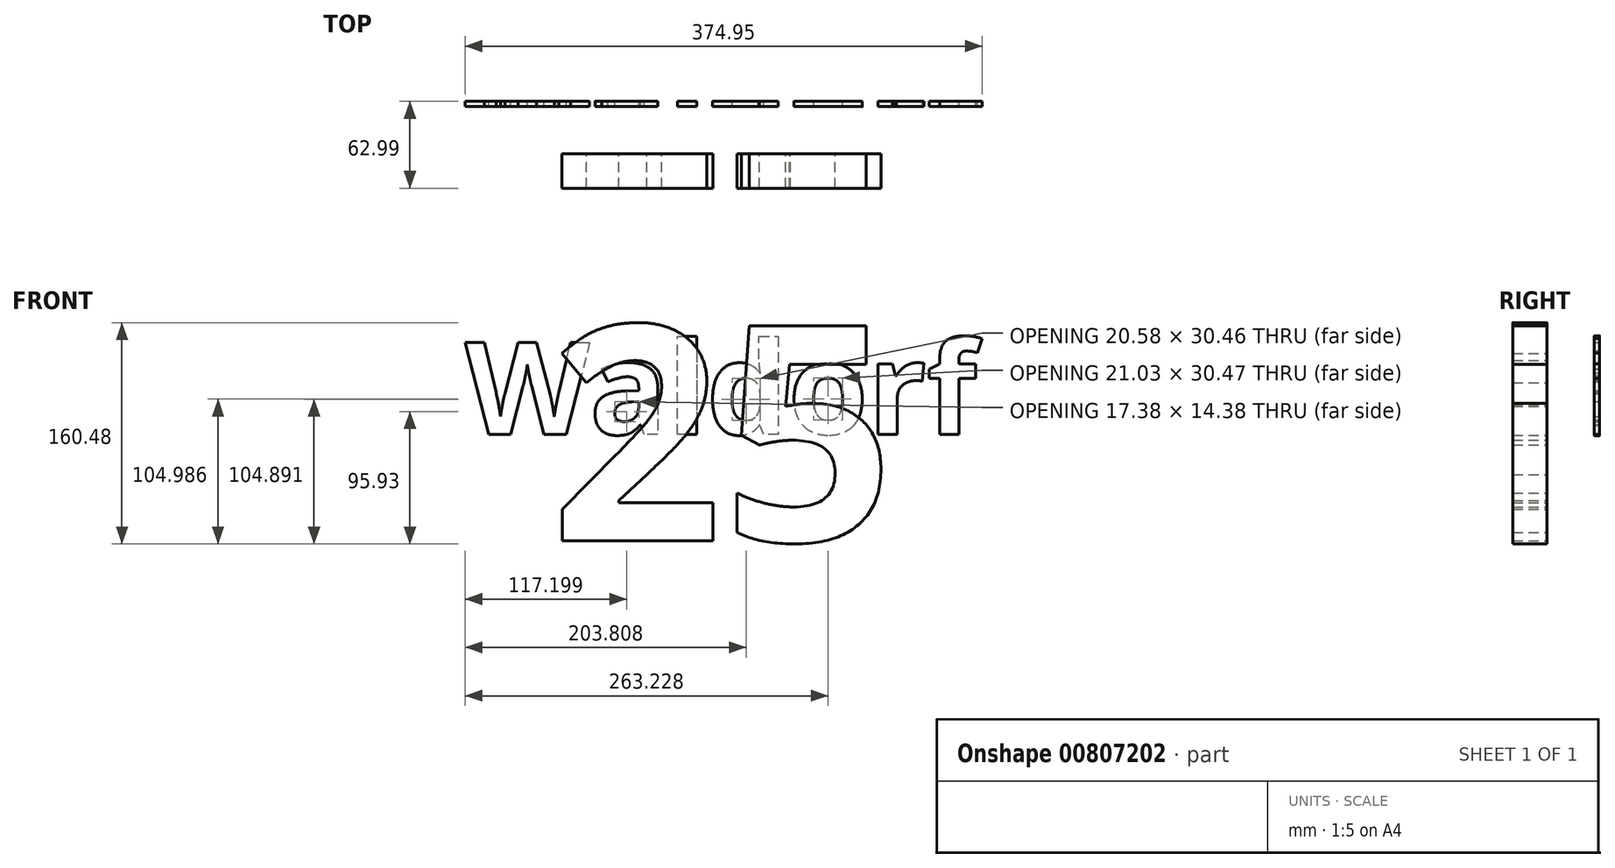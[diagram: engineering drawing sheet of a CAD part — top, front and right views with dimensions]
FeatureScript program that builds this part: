
annotation { "Feature Type Name" : "Feature", "Feature Type Description" : "" }
export const myFeature = defineFeature(function(context is Context, id is Id, definition is map)
    precondition{}
    {
        {
            var Q0;
            Q0=qCreatedBy(makeId("Front.planeOp"),FACE);
            var sketch = newSketch(context, id + "F0", { "sketchPlane" : qUnion([Q0])});
            skText(sketch, "E0", { "text": "Waldorf", "fontName": "NotoSans-Bold.ttf"});
            skText(sketch, "E1", { "text": "25", "fontName": "OpenSans-Bold.ttf"});
            const initialGuessF0  = {"E0": [-0.17587, 0.0215, 1, 0, 0.06725], "E1": [-0.11415, -0.15744, 1, 0, 0.15744]};
            skSetInitialGuess(sketch, initialGuessF0);
            skSolve(sketch);
        }
        {
            var Q0;
            Q0=makeQuery(id+"F0.imprint","IMPRINT",FACE,{"disambiguationData":[TD([[makeQuery(id+"F0.imprint","IMPRINT",EDGE,{"derivedFrom":sQuery(id+"F0.wireOp",EDGE,"E1.sketch_text.stroke-0")}),-1.0]])]});
            var Q1;
            Q1=makeQuery(id+"F0.imprint","IMPRINT",FACE,{"disambiguationData":[TD([[makeQuery(id+"F0.imprint","IMPRINT",EDGE,{"derivedFrom":sQuery(id+"F0.wireOp",EDGE,"E1.sketch_text.stroke-24")}),-1.0]])]});
            extrude(context, id + "F1", {"entities" : qUnion([Q0, Q1]), "depth" : 24.9 * mm, "offsetDistance" : 25.4 * mm});
        }
        {
            var Q0;
            Q0=makeQuery(id+"F0.imprint","IMPRINT",FACE,{"disambiguationData":[TD([[makeQuery(id+"F0.imprint","IMPRINT",EDGE,{"derivedFrom":sQuery(id+"F0.wireOp",EDGE,"E0.sketch_text.stroke-0")}),-1.0]])]});
            var Q1;
            Q1=makeQuery(id+"F0.imprint","IMPRINT",FACE,{"disambiguationData":[TD([[makeQuery(id+"F0.imprint","IMPRINT",EDGE,{"derivedFrom":sQuery(id+"F0.wireOp",EDGE,"E0.sketch_text.stroke-24")}),-1.0]])]});
            var Q2;
            Q2=makeQuery(id+"F0.imprint","IMPRINT",FACE,{"disambiguationData":[TD([[makeQuery(id+"F0.imprint","IMPRINT",EDGE,{"derivedFrom":sQuery(id+"F0.wireOp",EDGE,"E0.sketch_text.stroke-49")}),-1.0]])]});
            var Q3;
            Q3=makeQuery(id+"F0.imprint","IMPRINT",FACE,{"disambiguationData":[TD([[makeQuery(id+"F0.imprint","IMPRINT",EDGE,{"derivedFrom":sQuery(id+"F0.wireOp",EDGE,"E0.sketch_text.stroke-53")}),-1.0]])]});
            var Q4;
            Q4=makeQuery(id+"F0.imprint","IMPRINT",FACE,{"disambiguationData":[TD([[makeQuery(id+"F0.imprint","IMPRINT",EDGE,{"derivedFrom":sQuery(id+"F0.wireOp",EDGE,"E0.sketch_text.stroke-76")}),-1.0]])]});
            var Q5;
            Q5=makeQuery(id+"F0.imprint","IMPRINT",FACE,{"disambiguationData":[TD([[makeQuery(id+"F0.imprint","IMPRINT",EDGE,{"derivedFrom":sQuery(id+"F0.wireOp",EDGE,"E0.sketch_text.stroke-94")}),-1.0]])]});
            var Q6;
            Q6=makeQuery(id+"F0.imprint","IMPRINT",FACE,{"disambiguationData":[TD([[makeQuery(id+"F0.imprint","IMPRINT",EDGE,{"derivedFrom":sQuery(id+"F0.wireOp",EDGE,"E0.sketch_text.stroke-107")}),-1.0]])]});
            extrude(context, id + "F2", {"entities" : qUnion([Q0, Q1, Q2, Q3, Q4, Q5, Q6]), "operationType" : NewBodyOperationType.ADD, "depth" : 3.8 * mm, "offsetDistance" : 25.4 * mm});
        }
        {
            var Q0;
            Q0=makeQuery(id+"F1.opExtrude","SWEPT_BODY",BODY,{"disambiguationData":[OSD([sQuery(id+"F0.wireOp",EDGE,"E1.sketch_text.stroke-0"),sQuery(id+"F0.wireOp",EDGE,"E1.sketch_text.stroke-1"),sQuery(id+"F0.wireOp",EDGE,"E1.sketch_text.stroke-2"),sQuery(id+"F0.wireOp",EDGE,"E1.sketch_text.stroke-3"),sQuery(id+"F0.wireOp",EDGE,"E1.sketch_text.stroke-4"),sQuery(id+"F0.wireOp",EDGE,"E1.sketch_text.stroke-5"),sQuery(id+"F0.wireOp",EDGE,"E1.sketch_text.stroke-6"),sQuery(id+"F0.wireOp",EDGE,"E1.sketch_text.stroke-7"),sQuery(id+"F0.wireOp",EDGE,"E1.sketch_text.stroke-8"),sQuery(id+"F0.wireOp",EDGE,"E1.sketch_text.stroke-9"),sQuery(id+"F0.wireOp",EDGE,"E1.sketch_text.stroke-10"),sQuery(id+"F0.wireOp",EDGE,"E1.sketch_text.stroke-11"),sQuery(id+"F0.wireOp",EDGE,"E1.sketch_text.stroke-12"),sQuery(id+"F0.wireOp",EDGE,"E1.sketch_text.stroke-13"),sQuery(id+"F0.wireOp",EDGE,"E1.sketch_text.stroke-14"),sQuery(id+"F0.wireOp",EDGE,"E1.sketch_text.stroke-15"),sQuery(id+"F0.wireOp",EDGE,"E1.sketch_text.stroke-16"),sQuery(id+"F0.wireOp",EDGE,"E1.sketch_text.stroke-17"),sQuery(id+"F0.wireOp",EDGE,"E1.sketch_text.stroke-18"),sQuery(id+"F0.wireOp",EDGE,"E1.sketch_text.stroke-19"),sQuery(id+"F0.wireOp",EDGE,"E1.sketch_text.stroke-20"),sQuery(id+"F0.wireOp",EDGE,"E1.sketch_text.stroke-21"),sQuery(id+"F0.wireOp",EDGE,"E1.sketch_text.stroke-22"),sQuery(id+"F0.wireOp",EDGE,"E1.sketch_text.stroke-23")])]});
            var Q1;
            Q1=makeQuery(id+"F1.opExtrude","SWEPT_BODY",BODY,{"disambiguationData":[OSD([sQuery(id+"F0.wireOp",EDGE,"E1.sketch_text.stroke-24"),sQuery(id+"F0.wireOp",EDGE,"E1.sketch_text.stroke-25"),sQuery(id+"F0.wireOp",EDGE,"E1.sketch_text.stroke-26"),sQuery(id+"F0.wireOp",EDGE,"E1.sketch_text.stroke-27"),sQuery(id+"F0.wireOp",EDGE,"E1.sketch_text.stroke-28"),sQuery(id+"F0.wireOp",EDGE,"E1.sketch_text.stroke-29"),sQuery(id+"F0.wireOp",EDGE,"E1.sketch_text.stroke-30"),sQuery(id+"F0.wireOp",EDGE,"E1.sketch_text.stroke-31"),sQuery(id+"F0.wireOp",EDGE,"E1.sketch_text.stroke-32"),sQuery(id+"F0.wireOp",EDGE,"E1.sketch_text.stroke-33"),sQuery(id+"F0.wireOp",EDGE,"E1.sketch_text.stroke-34"),sQuery(id+"F0.wireOp",EDGE,"E1.sketch_text.stroke-35"),sQuery(id+"F0.wireOp",EDGE,"E1.sketch_text.stroke-36"),sQuery(id+"F0.wireOp",EDGE,"E1.sketch_text.stroke-37"),sQuery(id+"F0.wireOp",EDGE,"E1.sketch_text.stroke-38"),sQuery(id+"F0.wireOp",EDGE,"E1.sketch_text.stroke-39"),sQuery(id+"F0.wireOp",EDGE,"E1.sketch_text.stroke-40"),sQuery(id+"F0.wireOp",EDGE,"E1.sketch_text.stroke-41"),sQuery(id+"F0.wireOp",EDGE,"E1.sketch_text.stroke-42"),sQuery(id+"F0.wireOp",EDGE,"E1.sketch_text.stroke-43")])]});
            var Q2;
            Q2=qCreatedBy(makeId("Front.planeOp"),FACE);
            transform(context, id + "F3", {"entities" : qUnion([Q0, Q1]), "transformType" : TransformType.TRANSLATION_DISTANCE, "transformDirection" : qUnion([Q2]), "distance" : 38.1 * mm, "makeCopy" : false});
        }
        {
            var Q0;
            Q0=makeQuery(id+"F1.opExtrude","SWEPT_BODY",BODY,{"disambiguationData":[OSD([sQuery(id+"F0.wireOp",EDGE,"E1.sketch_text.stroke-0"),sQuery(id+"F0.wireOp",EDGE,"E1.sketch_text.stroke-1"),sQuery(id+"F0.wireOp",EDGE,"E1.sketch_text.stroke-2"),sQuery(id+"F0.wireOp",EDGE,"E1.sketch_text.stroke-3"),sQuery(id+"F0.wireOp",EDGE,"E1.sketch_text.stroke-4"),sQuery(id+"F0.wireOp",EDGE,"E1.sketch_text.stroke-5"),sQuery(id+"F0.wireOp",EDGE,"E1.sketch_text.stroke-6"),sQuery(id+"F0.wireOp",EDGE,"E1.sketch_text.stroke-7"),sQuery(id+"F0.wireOp",EDGE,"E1.sketch_text.stroke-8"),sQuery(id+"F0.wireOp",EDGE,"E1.sketch_text.stroke-9"),sQuery(id+"F0.wireOp",EDGE,"E1.sketch_text.stroke-10"),sQuery(id+"F0.wireOp",EDGE,"E1.sketch_text.stroke-11"),sQuery(id+"F0.wireOp",EDGE,"E1.sketch_text.stroke-12"),sQuery(id+"F0.wireOp",EDGE,"E1.sketch_text.stroke-13"),sQuery(id+"F0.wireOp",EDGE,"E1.sketch_text.stroke-14"),sQuery(id+"F0.wireOp",EDGE,"E1.sketch_text.stroke-15"),sQuery(id+"F0.wireOp",EDGE,"E1.sketch_text.stroke-16"),sQuery(id+"F0.wireOp",EDGE,"E1.sketch_text.stroke-17"),sQuery(id+"F0.wireOp",EDGE,"E1.sketch_text.stroke-18"),sQuery(id+"F0.wireOp",EDGE,"E1.sketch_text.stroke-19"),sQuery(id+"F0.wireOp",EDGE,"E1.sketch_text.stroke-20"),sQuery(id+"F0.wireOp",EDGE,"E1.sketch_text.stroke-21"),sQuery(id+"F0.wireOp",EDGE,"E1.sketch_text.stroke-22"),sQuery(id+"F0.wireOp",EDGE,"E1.sketch_text.stroke-23")])]});
            var Q1;
            Q1=makeQuery(id+"F1.opExtrude","SWEPT_BODY",BODY,{"disambiguationData":[OSD([sQuery(id+"F0.wireOp",EDGE,"E1.sketch_text.stroke-24"),sQuery(id+"F0.wireOp",EDGE,"E1.sketch_text.stroke-25"),sQuery(id+"F0.wireOp",EDGE,"E1.sketch_text.stroke-26"),sQuery(id+"F0.wireOp",EDGE,"E1.sketch_text.stroke-27"),sQuery(id+"F0.wireOp",EDGE,"E1.sketch_text.stroke-28"),sQuery(id+"F0.wireOp",EDGE,"E1.sketch_text.stroke-29"),sQuery(id+"F0.wireOp",EDGE,"E1.sketch_text.stroke-30"),sQuery(id+"F0.wireOp",EDGE,"E1.sketch_text.stroke-31"),sQuery(id+"F0.wireOp",EDGE,"E1.sketch_text.stroke-32"),sQuery(id+"F0.wireOp",EDGE,"E1.sketch_text.stroke-33"),sQuery(id+"F0.wireOp",EDGE,"E1.sketch_text.stroke-34"),sQuery(id+"F0.wireOp",EDGE,"E1.sketch_text.stroke-35"),sQuery(id+"F0.wireOp",EDGE,"E1.sketch_text.stroke-36"),sQuery(id+"F0.wireOp",EDGE,"E1.sketch_text.stroke-37"),sQuery(id+"F0.wireOp",EDGE,"E1.sketch_text.stroke-38"),sQuery(id+"F0.wireOp",EDGE,"E1.sketch_text.stroke-39"),sQuery(id+"F0.wireOp",EDGE,"E1.sketch_text.stroke-40"),sQuery(id+"F0.wireOp",EDGE,"E1.sketch_text.stroke-41"),sQuery(id+"F0.wireOp",EDGE,"E1.sketch_text.stroke-42"),sQuery(id+"F0.wireOp",EDGE,"E1.sketch_text.stroke-43")])]});
            var Q2;
            Q2=qCreatedBy(makeId("Top.planeOp"),FACE);
            transform(context, id + "F4", {"entities" : qUnion([Q0, Q1]), "transformType" : TransformType.TRANSLATION_DISTANCE, "transformDirection" : qUnion([Q2]), "distance" : 101.6 * mm, "makeCopy" : false});
        }
    });
